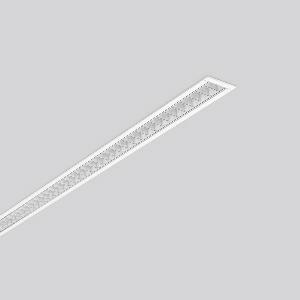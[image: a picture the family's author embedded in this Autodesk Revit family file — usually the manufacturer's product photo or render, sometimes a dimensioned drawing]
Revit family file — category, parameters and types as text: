
# Revit family: less_is_more_27_312179_002_1_2fd1
name_source: partatom
category: Lighting Fixtures
units: mm (PartAtom-declared; Revit-internal decimal feet)

## family parameters
Cut with Voids When Loaded = No
Host = Face
Light Source = No
Part Type = Normal
Room Calculation Point = No
Round Connector Dimension = Use Diameter
Shared = No

## types (1)
- LESS IS MORE 27 (1 x LED Modul 840, 3500 lm, 4000)
    Apparent Load = 39 VA
    CIE Flux Codes = 90 99 100 100 100
    Color Rendering = 80
    Color Temperature = 4000
    Default Elevation = 1800 mm
    Description = Series: LESS IS MORE 27
Recessed ceiling and wall luminaire with slim design. Housing: extruded aluminium profile, powder-coated. End cap aluminium powder-coated. High polish aluminium micro grid. Perfect for office areas (RUG < 19) and environments with computer screens in accordance with EN 12464-1. Suitable for Recessed ceiling mounting, wall (recessed). External driver with connecting cable. 
Colour: traffic white, matt (RAL 9016)
Length: 1514 mm
Width: 38 mm
Height: 2 mm
Cut-out length: 1506 mm
Cut-out width: 30 mm
Recess height: 45-60 mm
Luminaire: recess height: 37 mm
Lamp: LED
Socket: without socket
Colour temperature: 4000K
Colour rendering index (CRI): 82
System power: 39 W
Rated luminous flux: 3500 lm
Luminous efficiency: 90 lm/W
Control gear: Regulated power supply
Protection class: II
Type of protection: IP 20
    Height = 0 mm  [stored 0 ft]
    Lamp = 1 x LED Modul 840
    Lamp Light Flux = 3500 lm
    Lamp count = 1
    Length = 1514 mm
    Lifetime = 50000 h
    Luminous efficacy = 90 lm/W
    Manufacturer = RZB
    ModVariant = No
    Model = 312179.002.1
    Mounting Place = Ceiling, Wall
    Mounting Type = Recessed
    Number of Poles = 1
    OnlyDefault = Yes
    Power Factor = 1
    Product Name = LESS IS MORE 27
    Product group = Recessed LED linear luminaires
    ProductGroupID = 407
    Protection Class = Protection class II
    Protection Degree = IP 20
    RLX_Detail_Level = 1
    RLX_Emergency_Light_Flux = 0 lm
    RLX_Emergency_Type = 0
    RLX_Emergency_Type_DB = No
    RlxData = <blob elided: 27025 chars, md5=75b52f3e>
    Socket = socket
    Standby Power = 0 W
    System Light Flux = 3500 lm
    System Power = 39 W
    Type Comments = Product without accessories
    Type Image = 312177.002.jpg
    URL = http://relux.com
    VarID = ---
    Voltage = 230 V
    Voltage Range = 220-240 V
    Weight = 0.00 kg
    Width = 38 mm

note: [stored X ft] marks values corroborated as IEEE doubles in the binary element streams (Revit-internal decimal feet)

## geometry (parser evidence)
native form markers: Blend x4, Sweep x11
no freeform markers — native parametric forms only
